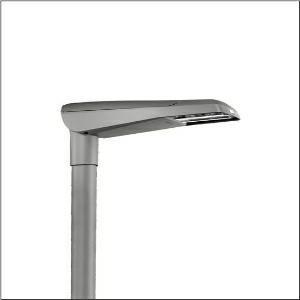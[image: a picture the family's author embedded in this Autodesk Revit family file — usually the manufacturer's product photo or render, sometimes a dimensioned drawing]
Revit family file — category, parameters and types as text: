
# Revit family: streetlight_sl_11_iq_micro___st1_2a_5xc1a41e08ce_a543
name_source: partatom
category: Lighting Fixtures
units: mm (PartAtom-declared; Revit-internal decimal feet)

## family parameters
Cut with Voids When Loaded = No
Host = Face
Light Source = No
Part Type = Normal
Room Calculation Point = No
Round Connector Dimension = Use Diameter
Shared = No

## types (1)
- --- (1 x LED, 1960 lm, 12.6 W, 4000K)
    Apparent Load = 13 VA
    CIE Flux Codes = 33 71 96 100 100
    Color Rendering = 70
    Color Temperature = 4000K
    Default Elevation = 1800 mm
    Description = Streetlight SL 11 iQ micro, mast luminaire, primary light control with 3 zone facetted reflector, of plastic, silver coated, highly specular, primary optical cover: cover, of PMMA, transparent, light distribution: ST1.2a, light emission: direct distribution, primary light characteristic: asymmetric, installation type: post-top, side-entry, lamps: LED, High Power LED, rated values: 1.960lm | 12,6W | 155,6lm/W (begin service life); end service life: 1.960lm | 12,9W; at 50% lumin. flux: 980lm | 6,8W | 144,1lm/W, colour temperature: 4000K, colour rendering: CRI > 70, light colour: 740, light setting 1 begin service life: 100% | 1.960lm | 12,6W | 155,6lm/W | 4.000K, light setting 1 end service life: 12,9W, further light settings possible, control: optimised constant luminous flux control (CLO 2.0), Desk-Remote (wireless, voltage-free reading and setting of iQ features in the workshop via application-optimized NFC function/RFID function), Light-Fading, Smart-Wire, Night-Set, Lumen-Switch, Temp-Guard, Auto-Match, with cable H07RN-F 5x 1.5mm², mains connection: 230..240V, AC, 50/60Hz, connection cable pre-assembled, cable length: 5,5m, luminaire housing, of diecast aluminium, powder-coated, Siteco® metallic grey (DB 702S), please order mast flange separately, inclination adjustable without tools: 0°, 5°, 10°, 15° (post-top) | 0°, -5°, -10°, -15° (side-entry), sealing non-destructively replaceable, multi-level sealing system, length: 600mm, width: 174mm, height: 116mm, mast flange for spigot size: 42mm (side-entry): 5XC10008XM4, 60/48mm (side-entry/post-top): 5XC10108XM2, 76/60mm (side-entry/post-top): 5XC10108XM1, equipment: standard, protection rating (complete): IP66, insulation class (complete): insulation class II (safety insulation), certification: CE, ENEC, ENEC+, VDE, impact resistance: IK10, permissible operating ambient temperature for outdoor applications: -25..+50°C, standard-compliant lighting for roads and squares, Environmental Product Declaration (EPD) tested and certified by an independent institute, packaging unit: 1 piece

Light Distribution: ST1.2a
    Height = 116 mm
    Lamp = 1 x LED
    Lamp Light Flux = 1960 lm
    Lamp Power = 12.6 W
    Lamp count = 1
    Length = 600 mm
    Luminous efficacy = 156 lm/W
    Manufacturer = Siteco
    ModVariant = No
    Model = 5XC1A41E08CE
    Number of Poles = 1
    OnlyDefault = Yes
    Power Factor = 1
    Product Name = Streetlight SL 11 iQ micro | ST1.2a
    Product group = mast luminaire | pylon top
    ProductGroupID = 6100
    Protection Class = Protection class II
    Protection Degree = IP 66
    RLX_Detail_Level = 1
    RLX_Emergency_Light_Flux = 0 lm
    RLX_Emergency_Type = 0
    RLX_Emergency_Type_DB = No
    RlxData = <blob elided: 26501 chars, md5=74c45b02>
    Socket = socket
    Standby Power = 0 W
    System Light Flux = 1960 lm
    System Power = 13 W
    Type Comments = factory setting: luminous flux: 100 % | dim-lin: 254 | 229 mA
    Type Image = l_1006566.jpg
    URL = http://relux.com
    VarID = @adj_001061
    Voltage = 0 V
    Weight = 0.00 kg
    Width = 174 mm

## geometry (parser evidence)
native form markers: Blend x4, Sweep x11
no freeform markers — native parametric forms only
